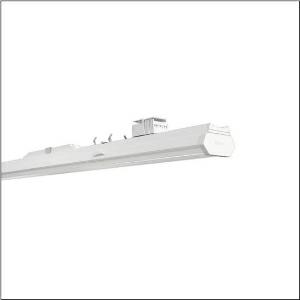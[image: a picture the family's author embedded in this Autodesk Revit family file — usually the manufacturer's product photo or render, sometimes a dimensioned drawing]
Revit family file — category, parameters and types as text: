
# Revit family: licross_r__11_protected_ho_51ts12vn4cxl_cde7
name_source: partatom
category: Lighting Fixtures
units: mm (PartAtom-declared; Revit-internal decimal feet)

## family parameters
Cut with Voids When Loaded = No
Host = Face
Light Source = No
Part Type = Normal
Room Calculation Point = No
Round Connector Dimension = Use Diameter
Shared = No

## types (1)
- --- (1 x LED, 12430 lm, 79.4 W, 4000K)
    Apparent Load = 79 VA
    CIE Flux Codes = 54 82 95 97 100
    Color Rendering = 80
    Color Temperature = 4000K
    Default Elevation = 1800 mm
    Description = Licross® 11 Protected HO, luminaire insert, of sheet steel, galvanised, coil coated, white, length: 1.500mm, width: 90mm, height: 101mm, LED rated luminous flux: 12.430lm, light colour: 840, control gear: DALI 2, CLO, control gear: ECG DALI, with plug, 5-pole, with phase selection, mains connection: 220..240V, AC, 50/60Hz, halogen-free wiring, primary optical cover: cover, of PMMA, light emission: direct with ceiling illumination distribution, protection rating (complete): IP50, insulation class (complete): insulation class I (protective earthing), certification: CE, ENEC, VDE, UKCA, protection symbol: D if used in an environment with non-conductive dust loads with corresponding accessories, permissible ambient temperature for indoor applications: -25..+30°C, corresponds to IFS (International Featured Standards) requirements for safety and quality in the food industry, reducing of maximum allowable ambient temperature of 5°C with ceiling mounting, packaging unit: 1 piece
    Height = 92 mm
    Lamp = 1 x LED
    Lamp Light Flux = 12430 lm
    Lamp Power = 79.4 W
    Lamp count = 1
    Length = 1500 mm
    Luminous efficacy = 157 lm/W
    Manufacturer = Siteco
    ModVariant = No
    Model = 51TS12VN4CXL
    Mounting Place = Ceiling
    Mounting Type = Pendant
    Number of Poles = 1
    OnlyDefault = Yes
    Power Factor = 1
    Product Name = Licross® 11 Protected HO
    Product group = luminaire insert
    ProductGroupID = 902
    Protection Class = Protection class I
    Protection Degree = IP 50
    RLX_Detail_Level = 1
    RlxData = <blob elided: 24209 chars, md5=ea60216e>
    Socket = socket
    Standby Power = 0 W
    System Light Flux = 12430 lm
    System Power = 79 W
    Type Comments = factory setting: luminous flux: 100 % | dim-lin: 254 | 448 mA
    Type Image = l_1256145.jpg
    URL = http://relux.com
    VarID = @adj_128481
    Voltage = 0 V
    Weight = 0.00 kg
    Width = 88 mm

## geometry (parser evidence)
native form markers: Blend x4, Sweep x11
no freeform markers — native parametric forms only
